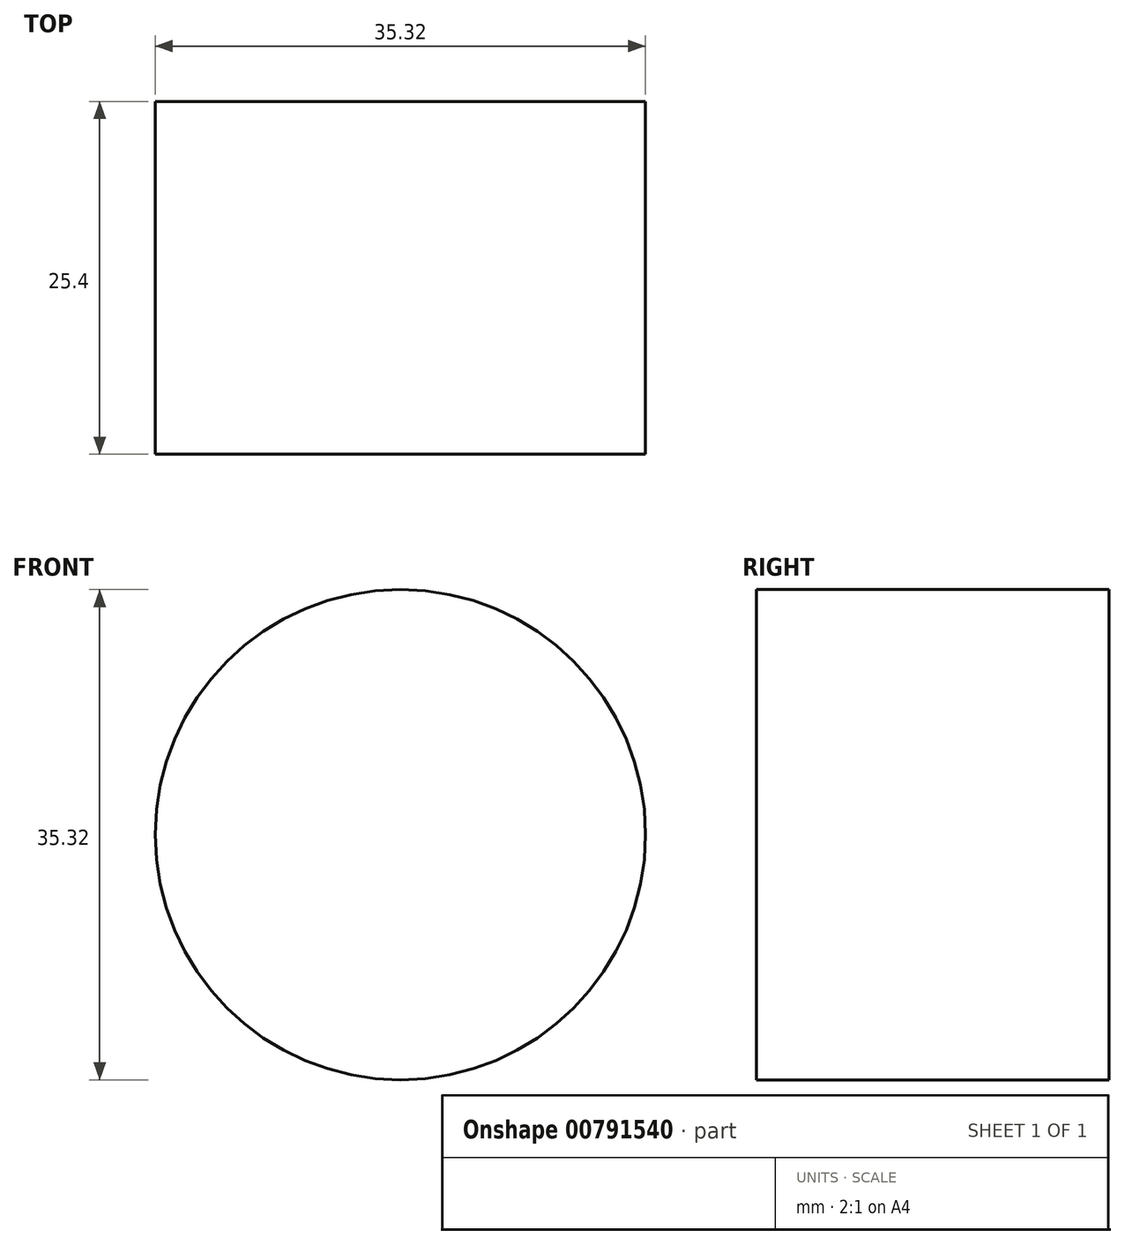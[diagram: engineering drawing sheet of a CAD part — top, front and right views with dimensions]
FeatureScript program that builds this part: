
annotation { "Feature Type Name" : "Feature", "Feature Type Description" : "" }
export const myFeature = defineFeature(function(context is Context, id is Id, definition is map)
    precondition{}
    {
        {
            var Q0;
            Q0=qCreatedBy(makeId("Front.planeOp"),FACE);
            var sketch = newSketch(context, id + "F0", { "sketchPlane" : qUnion([Q0])});
            skCircle(sketch, "E0", {"center": v(-18.8, 31.2) * mm, "radius": 17.66 * mm});
            skSolve(sketch);
        }
        {
            var Q0;
            Q0=makeQuery(id+"F0.imprint","IMPRINT",FACE,{"disambiguationData":[TD([[makeQuery(id+"F0.imprint","IMPRINT",EDGE,{"derivedFrom":sQuery(id+"F0.wireOp",EDGE,"E0")}),1.0]])]});
            extrude(context, id + "F1", {"entities" : qUnion([Q0]), "depth" : 25.4 * mm, "offsetDistance" : 25.4 * mm});
        }
    });
